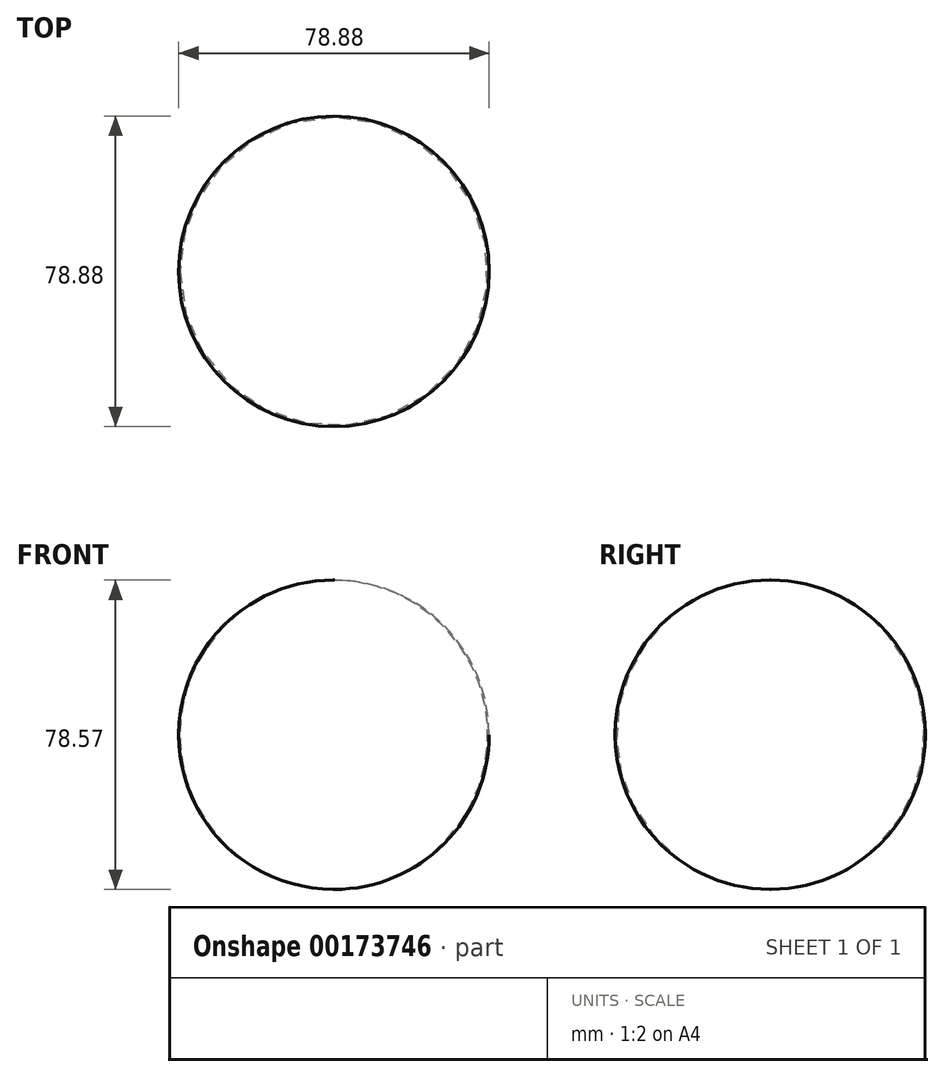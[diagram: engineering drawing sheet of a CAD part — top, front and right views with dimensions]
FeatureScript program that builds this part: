
annotation { "Feature Type Name" : "Feature", "Feature Type Description" : "" }
export const myFeature = defineFeature(function(context is Context, id is Id, definition is map)
    precondition{}
    {
        {
            var Q0;
            Q0=qCreatedBy(makeId("Front.planeOp"),FACE);
            var sketch = newSketch(context, id + "F0", { "sketchPlane" : qUnion([Q0])});
            skLineSegment(sketch, "E0", {"start": v(0, 40.58) * mm, "end": v(0, -38) * mm});
            skArc(sketch, "E1", {"start": v(0, -38) * mm, "mid": v(39.13, 1.3) * mm, "end": v(0, 40.58) * mm});
            skSolve(sketch);
        }
        {
            var Q0;
            Q0 = qSketchRegion(id + "F0", true);
            var Q1;
            Q1=sQuery(id+"F0.wireOp",EDGE,"E0");
            revolve(context, id + "F1", {"entities" : qUnion([Q0]), "axis" : qUnion([Q1]), "revolveType" : RevolveType.FULL});
        }
    });
